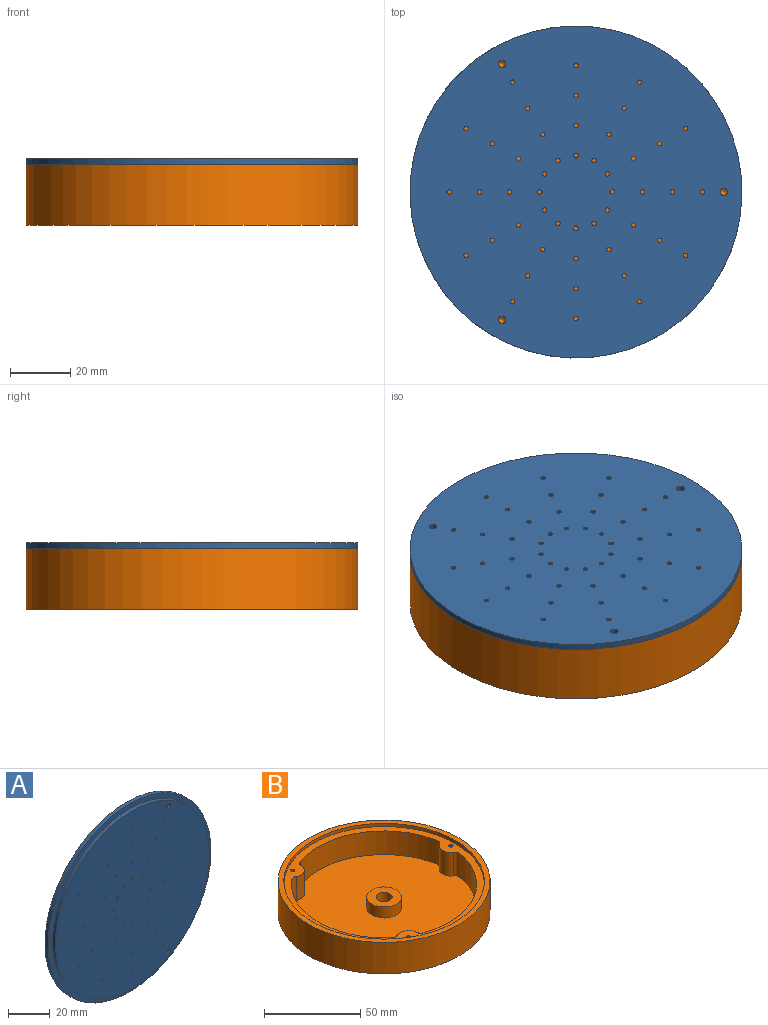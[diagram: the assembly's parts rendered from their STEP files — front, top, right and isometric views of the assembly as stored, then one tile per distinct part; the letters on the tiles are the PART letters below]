
ASSEMBLY  parts=2 mates=1
PART A: 56 faces, bbox 110x4x110 mm
  f0: cylinder r=1.25mm len=4mm, axis (0,1,0), area 31.4mm2, adj f49,f53
  f1: cylinder r=1.25mm len=4mm, axis (0,1,0), area 31.4mm2, adj f49,f53
  f2: cylinder r=0.75mm len=4mm, axis (0,1,0), area 18.8mm2, adj f49,f53
  f3: cylinder r=0.75mm len=4mm, axis (0,1,0), area 18.8mm2, adj f49,f53
  f4: cylinder r=0.75mm len=4mm, axis (0,1,0), area 18.8mm2, adj f49,f53
  f5: cylinder r=0.75mm len=4mm, axis (0,1,0), area 18.8mm2, adj f49,f53
  f6: cylinder r=0.75mm len=4mm, axis (0,1,0), area 18.8mm2, adj f49,f53
  f7: cylinder r=0.75mm len=4mm, axis (0,1,0), area 18.8mm2, adj f49,f53
  f8: cylinder r=0.75mm len=4mm, axis (0,1,0), area 18.8mm2, adj f49,f53
  f9: cylinder r=0.75mm len=4mm, axis (0,1,0), area 18.8mm2, adj f49,f53
  f10: cylinder r=0.75mm len=4mm, axis (0,1,0), area 18.8mm2, adj f49,f53
  f11: cylinder r=0.75mm len=4mm, axis (0,1,0), area 18.8mm2, adj f49,f53
  f12: cylinder r=0.75mm len=4mm, axis (0,1,0), area 18.8mm2, adj f49,f53
  f13: cylinder r=0.75mm len=4mm, axis (0,1,0), area 18.8mm2, adj f49,f53
  f14: cylinder r=0.75mm len=4mm, axis (0,1,0), area 18.8mm2, adj f49,f53
  f15: cylinder r=0.75mm len=4mm, axis (0,1,0), area 18.8mm2, adj f49,f53
  f16: cylinder r=0.75mm len=4mm, axis (0,1,0), area 18.8mm2, adj f49,f53
  f17: cylinder r=0.75mm len=4mm, axis (0,1,0), area 18.8mm2, adj f49,f53
  f18: cylinder r=0.75mm len=4mm, axis (0,1,0), area 18.8mm2, adj f49,f53
  f19: cylinder r=0.75mm len=4mm, axis (0,1,0), area 18.8mm2, adj f49,f53
  f20: cylinder r=0.75mm len=4mm, axis (0,1,0), area 18.8mm2, adj f49,f53
  f21: cylinder r=0.75mm len=4mm, axis (0,1,0), area 18.8mm2, adj f49,f53
  f22: cylinder r=0.75mm len=4mm, axis (0,1,0), area 18.8mm2, adj f49,f53
  f23: cylinder r=0.75mm len=4mm, axis (0,1,0), area 18.8mm2, adj f49,f53
  f24: cylinder r=0.75mm len=4mm, axis (0,1,0), area 18.8mm2, adj f49,f53
  f25: cylinder r=0.75mm len=4mm, axis (0,1,0), area 18.8mm2, adj f49,f53
  f26: cylinder r=0.75mm len=4mm, axis (0,1,0), area 18.8mm2, adj f49,f53
  f27: cylinder r=0.75mm len=4mm, axis (0,1,0), area 18.8mm2, adj f49,f53
  f28: cylinder r=0.75mm len=4mm, axis (0,1,0), area 18.8mm2, adj f49,f53
  f29: cylinder r=0.75mm len=4mm, axis (0,1,0), area 18.8mm2, adj f49,f53
  f30: cylinder r=0.75mm len=4mm, axis (0,1,0), area 18.8mm2, adj f49,f53
  f31: cylinder r=0.75mm len=4mm, axis (0,1,0), area 18.8mm2, adj f49,f53
  f32: cylinder r=0.75mm len=4mm, axis (0,1,0), area 18.8mm2, adj f49,f53
  f33: cylinder r=0.75mm len=4mm, axis (0,1,0), area 18.8mm2, adj f49,f53
  f34: cylinder r=0.75mm len=4mm, axis (0,1,0), area 18.8mm2, adj f49,f53
  f35: cylinder r=0.75mm len=4mm, axis (0,1,0), area 18.8mm2, adj f49,f53
  f36: cylinder r=0.75mm len=4mm, axis (0,1,0), area 18.8mm2, adj f49,f53
  f37: cylinder r=0.75mm len=4mm, axis (0,1,0), area 18.8mm2, adj f49,f53
  f38: cylinder r=0.75mm len=4mm, axis (0,1,0), area 18.8mm2, adj f49,f53
  f39: cylinder r=0.75mm len=4mm, axis (0,1,0), area 18.8mm2, adj f49,f53
  f40: cylinder r=0.75mm len=4mm, axis (0,1,0), area 18.8mm2, adj f49,f53
  f41: cylinder r=0.75mm len=4mm, axis (0,1,0), area 18.8mm2, adj f49,f53
  f42: cylinder r=0.75mm len=4mm, axis (0,1,0), area 18.8mm2, adj f49,f53
  f43: cylinder r=0.75mm len=4mm, axis (0,1,0), area 18.8mm2, adj f49,f53
  f44: cylinder r=0.75mm len=4mm, axis (0,1,0), area 18.8mm2, adj f49,f53
  f45: cylinder r=0.75mm len=4mm, axis (0,1,0), area 18.8mm2, adj f49,f53
  f46: cylinder r=0.75mm len=4mm, axis (0,1,0), area 18.8mm2, adj f49,f53
  f47: cylinder r=0.75mm len=4mm, axis (0,1,0), area 18.8mm2, adj f49,f53
  f48: cylinder r=0.75mm len=4mm, axis (0,1,0), area 18.8mm2, adj f49,f53
  f49: plane 104x104mm, normal (0,-1,0), area 8395.3mm2, adj f0,f1,f2,f3,f4,f5,f6,f7
  f50: cylinder r=52mm len=104mm, axis (0,1,0), area 653.5mm2, adj f49,f51
  f51: plane 110x110mm, normal (0,-1,0), area 1008.5mm2, adj f50,f52
  f52: cylinder r=55mm len=110mm, axis (0,1,0), area 691.2mm2, adj f51,f53
  f53: plane 110x110mm, normal (0,1,0), area 9403.8mm2, adj f0,f1,f2,f3,f4,f5,f6,f7
  f54: cylinder r=0.75mm len=4mm, axis (0,1,0), area 18.8mm2, adj f49,f53
  f55: cylinder r=1.25mm len=4mm, axis (0,1,0), area 31.4mm2, adj f49,f53
PART B: 27 faces, bbox 110x110x20 mm
  f0: plane 96x95.34mm, normal (0,0,1), area 6848.6mm2, adj f1,f2,f7,f10,f12,f13,f14,f21
  f1: cylinder r=6mm len=15mm, axis (0,0,-1), area 184.7mm2, adj f0,f9,f21,f22
  f2: cylinder r=6mm len=15mm, axis (0,0,-1), area 184.7mm2, adj f0,f9,f23,f24
  f3: cylinder r=52mm len=104mm, axis (0,0,-1), area 653.5mm2, adj f5,f9
  f4: cylinder r=55mm len=110mm, axis (0,0,-1), area 6911.5mm2, adj f5,f6
  f5: plane 110x110mm, normal (0,0,1), area 1008.5mm2, adj f3,f4
  f6: plane 110x110mm, normal (0,0,-1), area 9448.8mm2, adj f4,f11
  f7: cylinder r=9mm len=18mm, axis (0,0,-1), area 395.8mm2, adj f0,f8
  f8: plane 18x18mm, normal (0,0,1), area 199.9mm2, adj f7,f11
  f9: plane 104.11x104.01mm, normal (0,0,1), area 1380mm2, adj f1,f2,f3,f10,f12,f13,f14,f16
  f10: cylinder r=6mm len=15mm, axis (0,0,-1), area 184.7mm2, adj f0,f9,f25,f26
  f11: cylinder r=4.17mm len=10mm, axis (0,0,-1), area 261.8mm2, adj f6,f8
  f12: cylinder r=48mm len=63.83mm, axis (0,0,-1), area 1260.4mm2, adj f0,f9,f23,f26
  f13: cylinder r=48mm len=63.83mm, axis (0,0,-1), area 1260.4mm2, adj f0,f9,f22,f25
  f14: cylinder r=48mm len=73.7mm, axis (0,0,-1), area 1260.4mm2, adj f0,f9,f21,f24
  f15: cone r=0mm half-angle=59deg, axis (0,0,1), area 4.6mm2, adj f16
  f16: cylinder r=1.12mm len=10mm, axis (0,0,1), area 70.2mm2, adj f9,f15
  f17: cone r=0mm half-angle=59deg, axis (0,0,1), area 4.6mm2, adj f18
  f18: cylinder r=1.12mm len=10mm, axis (0,0,1), area 70.2mm2, adj f9,f17
  f19: cone r=0mm half-angle=59deg, axis (0,0,1), area 4.6mm2, adj f20
  f20: cylinder r=1.12mm len=10mm, axis (0,0,1), area 70.2mm2, adj f9,f19
  f21: cylinder r=3mm len=15mm, axis (0,0,-1), area 53.9mm2, adj f0,f1,f9,f14
  f22: cylinder r=3mm len=15mm, axis (0,0,1), area 53.9mm2, adj f0,f1,f9,f13
  f23: cylinder r=3mm len=15mm, axis (0,0,-1), area 53.9mm2, adj f0,f2,f9,f12
  f24: cylinder r=3mm len=15mm, axis (0,0,1), area 53.9mm2, adj f0,f2,f9,f14
  f25: cylinder r=3mm len=15mm, axis (0,0,-1), area 53.9mm2, adj f0,f9,f10,f13
  f26: cylinder r=3mm len=15mm, axis (0,0,1), area 53.9mm2, adj f0,f9,f10,f12
PLACE A rot(axis=(0.77,-0.45,-0.45),104.5deg) t=(-4.46,27.74,58)mm
PLACE B t=(-4.46,27.74,40)mm fixed
MATE revolute B.f3 <-> A.f50  axis (0,0,1) through (-4.46,27.74,60)mm
